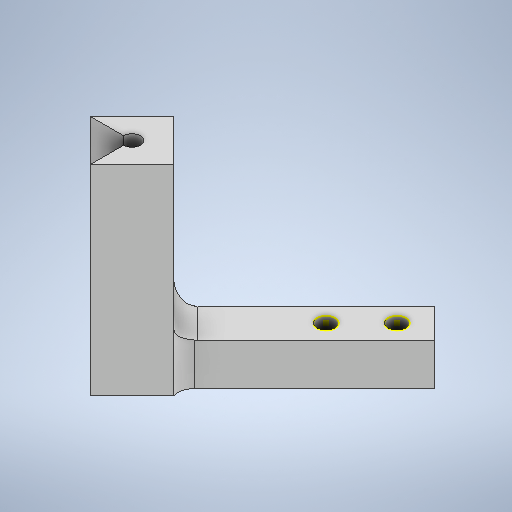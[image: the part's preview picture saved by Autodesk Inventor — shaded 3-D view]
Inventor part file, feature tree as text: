
AUTODESK INVENTOR PART (.ipt)
format: ipt  version: 2025.1 (Build 291241000, 241)  size: 645,632 bytes
history: native  units: in
note: dims shown in document units (in); Inventor stores cm internally (conversion verified against a paired STEP export)
features: sketch x3, extrude x2, fillet x2
ambient origin geometry x8: Origin, YZ Plane, XZ Plane, XY Plane, X Axis, Y Axis, Z Axis, Center Point
bodies: Solid1 (feature_tree)
feature tree (7):
  extrude  "Extrusion1"  Depth=0.8661in
  extrude  "Extrusion2"  Depth=0.0846in
  fillet  "Fillet1"  Radius=0.0984in
  fillet  "Fillet2"  Radius=0.1969in
  sketch  "Sketch3"  dims[d9=0.1969in d10=0.0in d11=0.0787in d12=0.0787in]
  sketch  "Sketch1"  dims[d0=0.9409in d1=0.0in d2=0.8661in]
  sketch  "Sketch2"  dims[d5=0.0846in d6=0.0846in d7=0.0984in d8=0.1969in]
